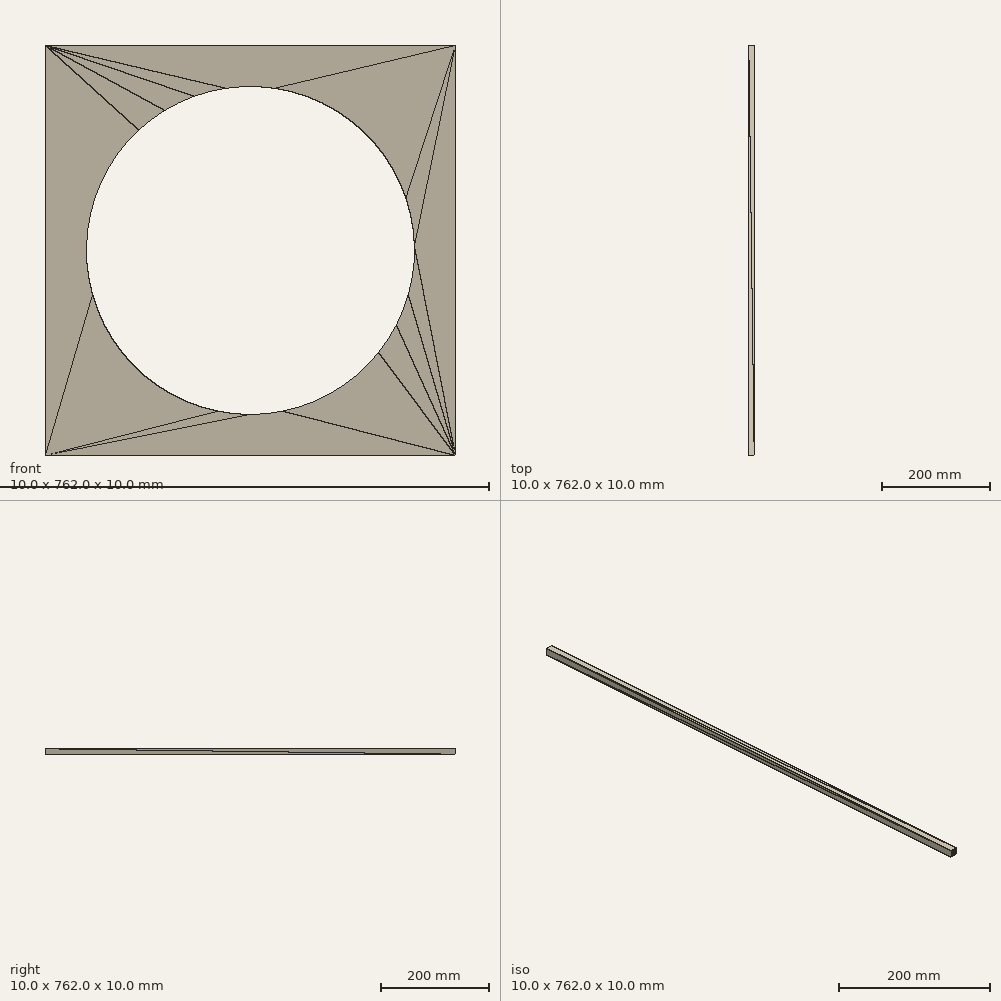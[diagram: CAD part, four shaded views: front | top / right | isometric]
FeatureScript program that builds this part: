
annotation { "Feature Type Name" : "Feature", "Feature Type Description" : "" }
export const myFeature = defineFeature(function(context is Context, id is Id, definition is map)
    precondition{}
    {
        {
            var Q0;
            Q0=qCreatedBy(makeId("Front.planeOp"),FACE);
            var sketch = newSketch(context, id + "F0", { "sketchPlane" : qUnion([Q0])});
            skLineSegment(sketch, "E0.bottom", {"start": v(5, 5) * mm, "end": v(-5, 5) * mm});
            skLineSegment(sketch, "E0.top", {"start": v(5, -5) * mm, "end": v(-5, -5) * mm});
            skLineSegment(sketch, "E0.left", {"start": v(5, 5) * mm, "end": v(5, -5) * mm});
            skLineSegment(sketch, "E0.right", {"start": v(-5, 5) * mm, "end": v(-5, -5) * mm});
            skPoint(sketch, "E0.middle", {"position": v(0, 0) * mm});
            skCircle(sketch, "E1", {"center": v(0, 0) * mm, "radius": 4 * mm});
            skSolve(sketch);
        }
        {
            var Q0;
            Q0=makeQuery(id+"F0.imprint","IMPRINT",FACE,{"disambiguationData":[TD([[makeQuery(id+"F0.imprint","IMPRINT",EDGE,{"derivedFrom":sQuery(id+"F0.wireOp",EDGE,"E0.bottom")}),1.0]])]});
            extrude(context, id + "F1", {"entities" : qUnion([Q0]), "depth" : 762 * mm, "offsetDistance" : 25.4 * mm});
        }
    });
